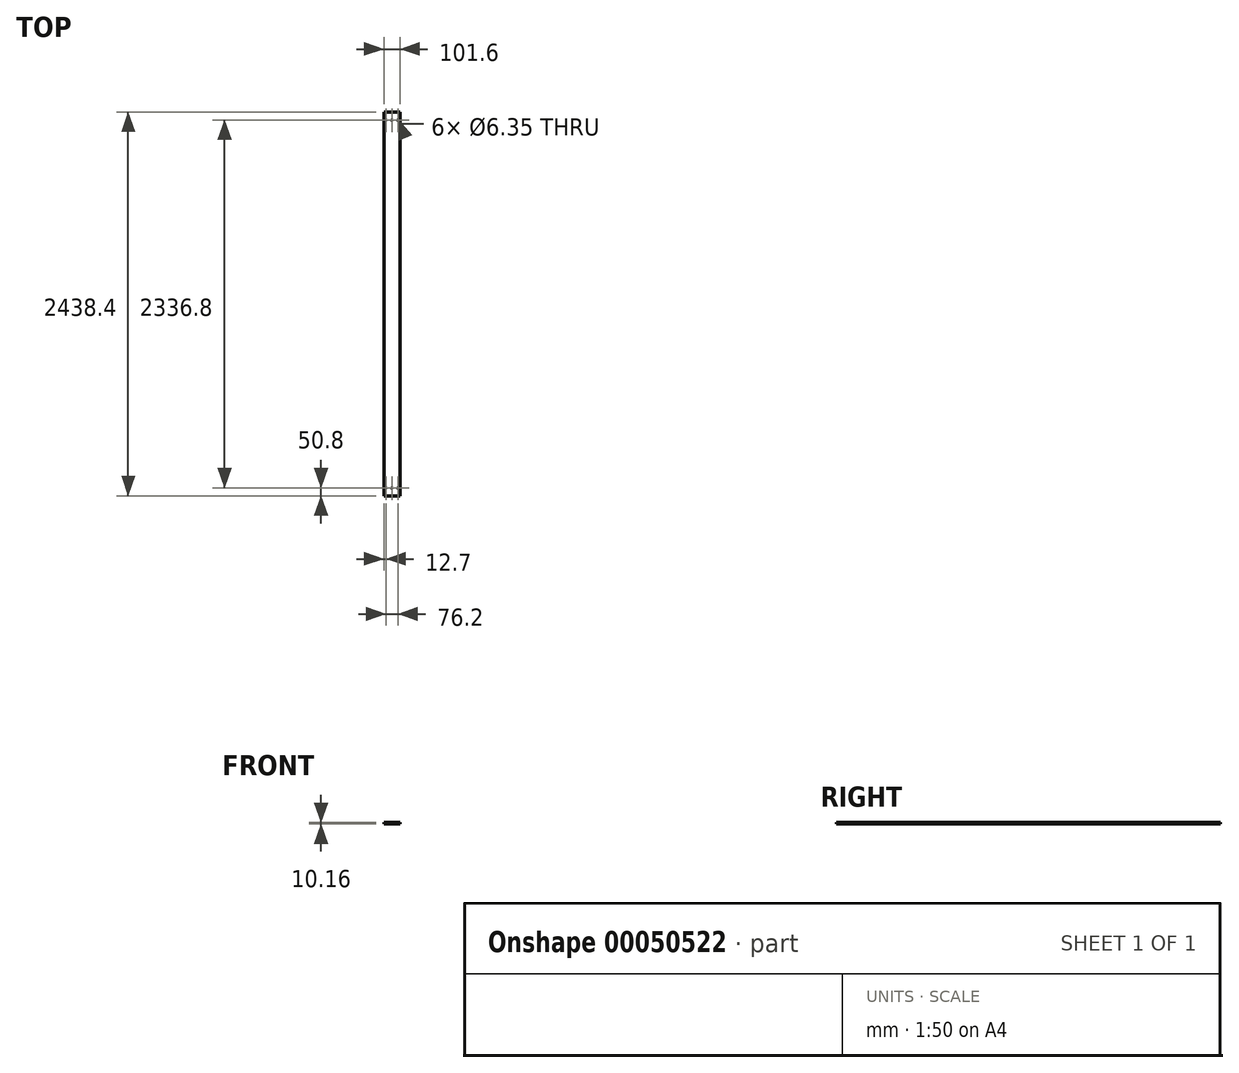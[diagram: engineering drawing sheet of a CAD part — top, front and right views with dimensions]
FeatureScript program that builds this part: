
annotation { "Feature Type Name" : "Feature", "Feature Type Description" : "" }
export const myFeature = defineFeature(function(context is Context, id is Id, definition is map)
    precondition{}
    {
        {
            var Q0;
            Q0=qCreatedBy(makeId("Top.planeOp"),FACE);
            var sketch = newSketch(context, id + "F0", { "sketchPlane" : qUnion([Q0])});
            skLineSegment(sketch, "E0.rect.bottom", {"start": v(50.8, 1219.2) * mm, "end": v(-50.8, 1219.2) * mm});
            skLineSegment(sketch, "E0.rect.top", {"start": v(50.8, -1219.2) * mm, "end": v(-50.8, -1219.2) * mm});
            skLineSegment(sketch, "E0.rect.left", {"start": v(50.8, 1219.2) * mm, "end": v(50.8, -1219.2) * mm});
            skLineSegment(sketch, "E0.rect.right", {"start": v(-50.8, 1219.2) * mm, "end": v(-50.8, -1219.2) * mm});
            skPoint(sketch, "E0.rect.middle", {"position": v(0, 0) * mm});
            skSolve(sketch);
        }
        {
            var Q0;
            Q0 = qSketchRegion(id + "F0", true);
            extrude(context, id + "F1", {"entities" : qUnion([Q0]), "endBound" : BoundingType.SYMMETRIC, "depth" : 10.16 * mm});
        }
        {
            var Q0;
            Q0=makeQuery(id+"F1.opExtrude","CAP_FACE",FACE,{"disambiguationData":[OSD([sQuery(id+"F0.wireOp",EDGE,"E0.rect.bottom"),sQuery(id+"F0.wireOp",EDGE,"E0.rect.top"),sQuery(id+"F0.wireOp",EDGE,"E0.rect.left"),sQuery(id+"F0.wireOp",EDGE,"E0.rect.right")])],"isStart":false});
            var sketch = newSketch(context, id + "F2", { "sketchPlane" : qUnion([Q0])});
            skCircle(sketch, "E1", {"center": v(0, -1168.4) * mm, "radius": 3.18 * mm});
            skCircle(sketch, "E2", {"center": v(0, 1168.4) * mm, "radius": 3.18 * mm});
            skPoint(sketch, "E2.centerSnap0", {"position": v(0, 1219.2) * mm});
            skLineSegment(sketch, "E3", {"start": v(0, 1168.4) * mm, "end": v(0, 0) * mm, "construction": true});
            skLineSegment(sketch, "E4", {"start": v(0, 0) * mm, "end": v(0, -1168.4) * mm, "construction": true});
            skCircle(sketch, "E5", {"center": v(-38.1, 1168.4) * mm, "radius": 3.18 * mm});
            skCircle(sketch, "E6", {"center": v(38.1, 1168.4) * mm, "radius": 3.18 * mm});
            skLineSegment(sketch, "E7.rect.bottom", {"start": v(-38.1, 1168.4) * mm, "end": v(38.1, 1168.4) * mm, "construction": true});
            skLineSegment(sketch, "E7.rect.top", {"start": v(-38.1, -1168.4) * mm, "end": v(38.1, -1168.4) * mm, "construction": true});
            skLineSegment(sketch, "E7.rect.left", {"start": v(-38.1, 1168.4) * mm, "end": v(-38.1, -1168.4) * mm, "construction": true});
            skLineSegment(sketch, "E7.rect.right", {"start": v(38.1, 1168.4) * mm, "end": v(38.1, -1168.4) * mm, "construction": true});
            skPoint(sketch, "E7.rect.middle", {"position": v(0, 0) * mm});
            skCircle(sketch, "E8", {"center": v(-38.1, -1168.4) * mm, "radius": 3.18 * mm});
            skCircle(sketch, "E9", {"center": v(38.1, -1168.4) * mm, "radius": 3.18 * mm});
            skSolve(sketch);
        }
        {
            var Q0;
            Q0 = qSketchRegion(id + "F2", true);
            extrude(context, id + "F3", {"entities" : qUnion([Q0]), "operationType" : NewBodyOperationType.REMOVE, "endBound" : BoundingType.SYMMETRIC, "oppositeDirection" : true, "depth" : 25.4 * mm});
        }
    });
